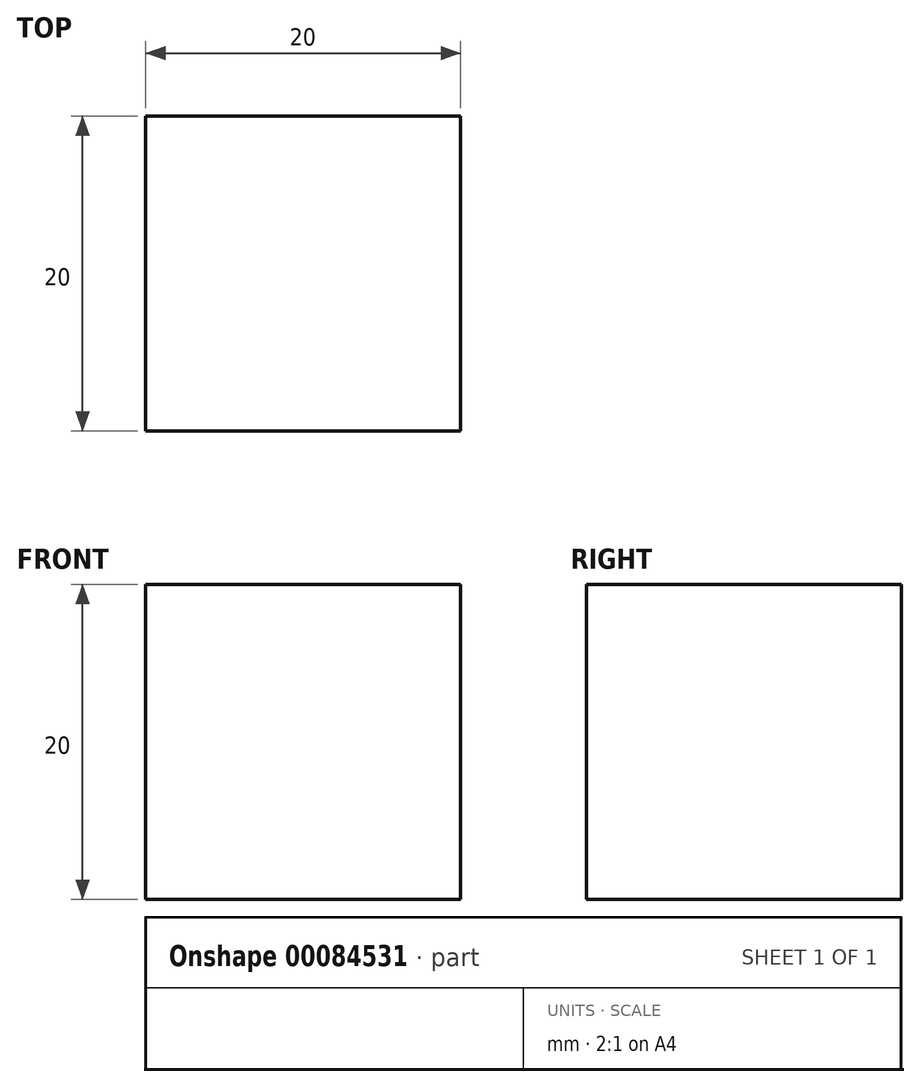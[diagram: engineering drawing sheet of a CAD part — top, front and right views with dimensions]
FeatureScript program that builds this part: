
annotation { "Feature Type Name" : "Feature", "Feature Type Description" : "" }
export const myFeature = defineFeature(function(context is Context, id is Id, definition is map)
    precondition{}
    {
        {
            var Q0;
            Q0=qCreatedBy(makeId("Top.planeOp"),FACE);
            var sketch = newSketch(context, id + "F0", { "sketchPlane" : qUnion([Q0])});
            skLineSegment(sketch, "E0.bottom", {"start": v(10, -10) * mm, "end": v(-10, -10) * mm});
            skLineSegment(sketch, "E0.top", {"start": v(10, 10) * mm, "end": v(-10, 10) * mm});
            skLineSegment(sketch, "E0.left", {"start": v(10, -10) * mm, "end": v(10, 10) * mm});
            skLineSegment(sketch, "E0.right", {"start": v(-10, -10) * mm, "end": v(-10, 10) * mm});
            skPoint(sketch, "E0.middle", {"position": v(0, 0) * mm});
            skSolve(sketch);
        }
        {
            var Q0;
            Q0 = qSketchRegion(id + "F0", true);
            extrude(context, id + "F1", {"entities" : qUnion([Q0]), "depth" : 20 * mm});
        }
    });
